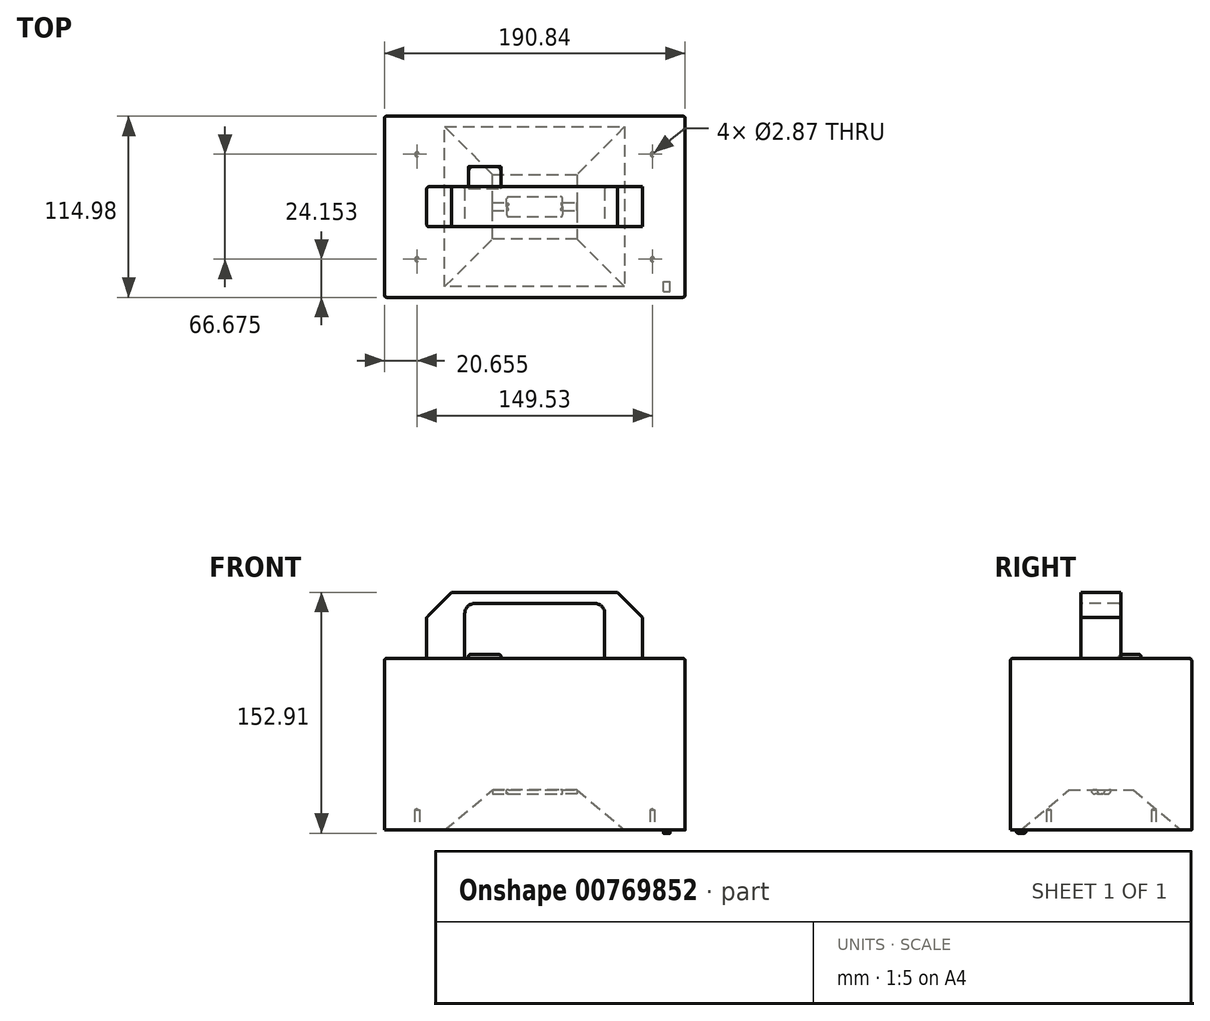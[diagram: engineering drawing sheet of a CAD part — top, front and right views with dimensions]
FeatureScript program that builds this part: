
annotation { "Feature Type Name" : "Feature", "Feature Type Description" : "" }
export const myFeature = defineFeature(function(context is Context, id is Id, definition is map)
    precondition{}
    {
        {
            var Q0;
            Q0=qCreatedBy(makeId("Top.planeOp"),FACE);
            var sketch = newSketch(context, id + "F0", { "sketchPlane" : qUnion([Q0])});
            skLineSegment(sketch, "E0.bottom", {"start": v(-95.42, 57.5) * mm, "end": v(95.42, 57.5) * mm});
            skLineSegment(sketch, "E0.top", {"start": v(-95.42, -57.5) * mm, "end": v(95.42, -57.5) * mm});
            skLineSegment(sketch, "E0.left", {"start": v(-95.42, 57.5) * mm, "end": v(-95.42, -57.5) * mm});
            skLineSegment(sketch, "E0.right", {"start": v(95.42, 57.5) * mm, "end": v(95.42, -57.5) * mm});
            skLineSegment(sketch, "E1", {"start": v(-95.42, 57.5) * mm, "end": v(95.42, -57.5) * mm, "construction": true});
            skSolve(sketch);
        }
        {
            var Q0;
            Q0 = qSketchRegion(id + "F0", true);
            extrude(context, id + "F1", {"entities" : qUnion([Q0]), "oppositeDirection" : true, "depth" : 108.97 * mm, "offsetDistance" : 25.4 * mm});
        }
        {
            var Q0;
            Q0=makeQuery(id+"F1.opExtrude","CAP_FACE",FACE,{"disambiguationData":[OSD([sQuery(id+"F0.wireOp",EDGE,"E0.bottom"),sQuery(id+"F0.wireOp",EDGE,"E0.top"),sQuery(id+"F0.wireOp",EDGE,"E0.left"),sQuery(id+"F0.wireOp",EDGE,"E0.right")])],"isStart":true});
            var sketch = newSketch(context, id + "F2", { "sketchPlane" : qUnion([Q0])});
            skLineSegment(sketch, "E2", {"start": v(-95.42, 0) * mm, "end": v(95.42, 0) * mm, "construction": true});
            skLineSegment(sketch, "E3.bottom", {"start": v(-68.58, 12.7) * mm, "end": v(68.58, 12.7) * mm});
            skLineSegment(sketch, "E3.top", {"start": v(-68.58, -12.7) * mm, "end": v(68.58, -12.7) * mm});
            skLineSegment(sketch, "E3.left", {"start": v(-68.58, 12.7) * mm, "end": v(-68.58, -12.7) * mm});
            skLineSegment(sketch, "E3.right", {"start": v(68.58, 12.7) * mm, "end": v(68.58, -12.7) * mm});
            skLineSegment(sketch, "E4", {"start": v(-68.58, 12.7) * mm, "end": v(68.58, -12.7) * mm, "construction": true});
            skPoint(sketch, "E5", {"position": v(0, 0) * mm});
            skSolve(sketch);
        }
        {
            var Q0;
            Q0 = qSketchRegion(id + "F2", true);
            extrude(context, id + "F3", {"entities" : qUnion([Q0]), "operationType" : NewBodyOperationType.ADD, "depth" : 41.9 * mm, "offsetDistance" : 25.4 * mm});
        }
        {
            var Q0;
            Q0=makeQuery(id+"F3.opExtrude","SWEPT_FACE",FACE,{"disambiguationData":[OSD([sQuery(id+"F2.wireOp",EDGE,"E3.top")])]});
            var sketch = newSketch(context, id + "F4", { "sketchPlane" : qUnion([Q0])});
            skLineSegment(sketch, "E6", {"start": v(-68.58, 26.03) * mm, "end": v(-52.7, 41.91) * mm});
            skLineSegment(sketch, "E7", {"start": v(-52.7, 41.91) * mm, "end": v(-68.58, 41.91) * mm});
            skLineSegment(sketch, "E8", {"start": v(-68.58, 41.91) * mm, "end": v(-68.58, 26.03) * mm});
            skLineSegment(sketch, "E9", {"start": v(68.58, 26.04) * mm, "end": v(52.7, 41.91) * mm});
            skLineSegment(sketch, "E10", {"start": v(52.7, 41.91) * mm, "end": v(68.58, 41.91) * mm});
            skLineSegment(sketch, "E11", {"start": v(68.58, 41.91) * mm, "end": v(68.58, 26.04) * mm});
            skLineSegment(sketch, "E12.bottom", {"start": v(-44.45, 0) * mm, "end": v(44.45, 0) * mm});
            skLineSegment(sketch, "E12.top", {"start": v(-44.45, 34.93) * mm, "end": v(44.45, 34.93) * mm});
            skLineSegment(sketch, "E12.left", {"start": v(-44.45, 0) * mm, "end": v(-44.45, 34.92) * mm});
            skLineSegment(sketch, "E12.right", {"start": v(44.45, 0) * mm, "end": v(44.45, 34.93) * mm});
            skLineSegment(sketch, "E13", {"start": v(0, 41.91) * mm, "end": v(0, 34.93) * mm, "construction": true});
            skSolve(sketch);
        }
        {
            var Q0;
            Q0 = qSketchRegion(id + "F4", true);
            extrude(context, id + "F5", {"entities" : qUnion([Q0]), "operationType" : NewBodyOperationType.REMOVE, "endBound" : BoundingType.THROUGH_ALL, "oppositeDirection" : true, "depth" : 25.4 * mm, "offsetDistance" : 25.4 * mm});
        }
        {
            var Q0;
            Q0=makeQuery(id+"F5.boolean.opBoolean","COPY",EDGE,{"derivedFrom":makeQuery(id+"F5.opExtrude","SWEPT_EDGE",EDGE,{"disambiguationData":[OSD([sQuery(id+"F2.wireOp",EDGE,"E3.top"),sQuery(id+"F2.wireOp",EDGE,"E3.left"),sQuery(id+"F4.wireOp",EDGE,"E6"),sQuery(id+"F4.wireOp",EDGE,"E8")])]})});
            var Q1;
            Q1=makeQuery(id+"F5.boolean.opBoolean","COPY",EDGE,{"derivedFrom":makeQuery(id+"F5.opExtrude","SWEPT_EDGE",EDGE,{"disambiguationData":[OSD([sQuery(id+"F2.wireOp",EDGE,"E3.top"),sQuery(id+"F4.wireOp",EDGE,"E6"),sQuery(id+"F4.wireOp",EDGE,"E7")])]})});
            var Q2;
            Q2=makeQuery(id+"F5.boolean.opBoolean","COPY",EDGE,{"derivedFrom":makeQuery(id+"F5.opExtrude","SWEPT_EDGE",EDGE,{"disambiguationData":[OSD([sQuery(id+"F2.wireOp",EDGE,"E3.top"),sQuery(id+"F4.wireOp",EDGE,"E9"),sQuery(id+"F4.wireOp",EDGE,"E10")])]})});
            var Q3;
            Q3=makeQuery(id+"F5.boolean.opBoolean","COPY",EDGE,{"derivedFrom":makeQuery(id+"F5.opExtrude","SWEPT_EDGE",EDGE,{"disambiguationData":[OSD([sQuery(id+"F2.wireOp",EDGE,"E3.top"),sQuery(id+"F2.wireOp",EDGE,"E3.right"),sQuery(id+"F4.wireOp",EDGE,"E9"),sQuery(id+"F4.wireOp",EDGE,"E11")])]})});
            var Q4;
            Q4=makeQuery(id+"F5.boolean.opBoolean","COPY",EDGE,{"derivedFrom":makeQuery(id+"F5.opExtrude","SWEPT_EDGE",EDGE,{"disambiguationData":[OSD([sQuery(id+"F4.wireOp",EDGE,"E12.top"),sQuery(id+"F4.wireOp",EDGE,"E12.left")])]})});
            var Q5;
            Q5=makeQuery(id+"F5.boolean.opBoolean","COPY",EDGE,{"derivedFrom":makeQuery(id+"F5.opExtrude","SWEPT_EDGE",EDGE,{"disambiguationData":[OSD([sQuery(id+"F4.wireOp",EDGE,"E12.top"),sQuery(id+"F4.wireOp",EDGE,"E12.right")])]})});
            fillet(context, id + "F6", {"entities" : qUnion([Q0, Q1, Q2, Q3, Q4, Q5]), "radius" : 6.35 * mm, "tangentPropagation" : true, "allowEdgeOverflow" : false});
        }
        {
            var Q0;
            Q0=makeQuery(id+"F1.opExtrude","CAP_FACE",FACE,{"disambiguationData":[OSD([sQuery(id+"F0.wireOp",EDGE,"E0.bottom"),sQuery(id+"F0.wireOp",EDGE,"E0.top"),sQuery(id+"F0.wireOp",EDGE,"E0.left"),sQuery(id+"F0.wireOp",EDGE,"E0.right")])],"isStart":false});
            var sketch = newSketch(context, id + "F7", { "sketchPlane" : qUnion([Q0])});
            skLineSegment(sketch, "E14.bottom", {"start": v(-57.15, 50.8) * mm, "end": v(57.15, 50.8) * mm});
            skLineSegment(sketch, "E14.top", {"start": v(-57.15, -50.8) * mm, "end": v(57.15, -50.8) * mm});
            skLineSegment(sketch, "E14.left", {"start": v(-57.15, 50.8) * mm, "end": v(-57.15, -50.8) * mm});
            skLineSegment(sketch, "E14.right", {"start": v(57.15, 50.8) * mm, "end": v(57.15, -50.8) * mm});
            skLineSegment(sketch, "E15", {"start": v(-95.42, 0) * mm, "end": v(95.42, 0) * mm, "construction": true});
            skLineSegment(sketch, "E16", {"start": v(-57.15, 0) * mm, "end": v(57.15, 0) * mm, "construction": true});
            skLineSegment(sketch, "E17", {"start": v(0, 50.8) * mm, "end": v(0, -50.8) * mm, "construction": true});
            skPoint(sketch, "E18", {"position": v(0, 0) * mm});
            skSolve(sketch);
        }
        {
            var Q0;
            Q0 = qSketchRegion(id + "F7", true);
            extrude(context, id + "F8", {"entities" : qUnion([Q0]), "operationType" : NewBodyOperationType.REMOVE, "oppositeDirection" : true, "depth" : 25.4 * mm, "offsetDistance" : 25.4 * mm, "hasDraft" : true, "draftAngle" : 50 * degree, "draftPullDirection" : true});
        }
        {
            var Q0;
            Q0=makeQuery(id+"F8.boolean.opBoolean","COPY",FACE,{"derivedFrom":makeQuery(id+"F8.opExtrude","CAP_FACE",FACE,{"disambiguationData":[OSD([sQuery(id+"F7.wireOp",EDGE,"E14.bottom"),sQuery(id+"F7.wireOp",EDGE,"E14.top"),sQuery(id+"F7.wireOp",EDGE,"E14.left"),sQuery(id+"F7.wireOp",EDGE,"E14.right")])],"isStart":false})});
            var sketch = newSketch(context, id + "F9", { "sketchPlane" : qUnion([Q0])});
            skLineSegment(sketch, "E19.bottom", {"start": v(-17.78, 6.35) * mm, "end": v(17.78, 6.35) * mm});
            skLineSegment(sketch, "E19.top", {"start": v(-17.78, -6.35) * mm, "end": v(17.78, -6.35) * mm});
            skLineSegment(sketch, "E19.left", {"start": v(-26.88, 2.54) * mm, "end": v(-26.88, -2.54) * mm});
            skLineSegment(sketch, "E19.right", {"start": v(26.88, 2.54) * mm, "end": v(26.88, -2.54) * mm});
            skLineSegment(sketch, "E20", {"start": v(-26.88, 2.54) * mm, "end": v(-17.78, 2.54) * mm});
            skLineSegment(sketch, "E21", {"start": v(17.78, 2.54) * mm, "end": v(26.88, 2.54) * mm});
            skLineSegment(sketch, "E22", {"start": v(-26.88, -2.54) * mm, "end": v(-17.78, -2.54) * mm});
            skLineSegment(sketch, "E23", {"start": v(17.78, -2.54) * mm, "end": v(26.88, -2.54) * mm});
            skLineSegment(sketch, "E24", {"start": v(-17.78, 2.54) * mm, "end": v(-17.78, 6.35) * mm});
            skLineSegment(sketch, "E25", {"start": v(17.78, 2.54) * mm, "end": v(17.78, 6.35) * mm});
            skLineSegment(sketch, "E26", {"start": v(-17.78, -2.54) * mm, "end": v(-17.78, -6.35) * mm});
            skLineSegment(sketch, "E27", {"start": v(17.78, -2.54) * mm, "end": v(17.78, -6.35) * mm});
            skPoint(sketch, "E28", {"position": v(-26.88, 0) * mm});
            skSolve(sketch);
        }
        {
            var Q0;
            Q0 = qSketchRegion(id + "F9", true);
            extrude(context, id + "F10", {"entities" : qUnion([Q0]), "operationType" : NewBodyOperationType.ADD, "depth" : 2.54 * mm, "offsetDistance" : 25.4 * mm});
        }
        {
            var Q0;
            Q0=makeQuery(id+"F10.opExtrude","CAP_EDGE",EDGE,{"disambiguationData":[OSD([sQuery(id+"F9.wireOp",EDGE,"E19.bottom")])],"isStart":false});
            var Q1;
            Q1=makeQuery(id+"F10.opExtrude","CAP_EDGE",EDGE,{"disambiguationData":[OSD([sQuery(id+"F9.wireOp",EDGE,"E19.top")])],"isStart":false});
            fillet(context, id + "F11", {"entities" : qUnion([Q0, Q1]), "radius" : 2.54 * mm, "tangentPropagation" : true, "allowEdgeOverflow" : false});
        }
        {
            var Q0;
            Q0=makeQuery(id+"F10.opExtrude","CAP_EDGE",EDGE,{"disambiguationData":[OSD([sQuery(id+"F9.wireOp",EDGE,"E20")])],"isStart":false});
            var Q1;
            Q1=makeQuery(id+"F10.opExtrude","CAP_EDGE",EDGE,{"disambiguationData":[OSD([sQuery(id+"F9.wireOp",EDGE,"E22")])],"isStart":false});
            var Q2;
            Q2=makeQuery(id+"F10.opExtrude","CAP_EDGE",EDGE,{"disambiguationData":[OSD([sQuery(id+"F9.wireOp",EDGE,"E23")])],"isStart":false});
            var Q3;
            Q3=makeQuery(id+"F10.opExtrude","CAP_EDGE",EDGE,{"disambiguationData":[OSD([sQuery(id+"F9.wireOp",EDGE,"E21")])],"isStart":false});
            fillet(context, id + "F12", {"entities" : qUnion([Q0, Q1, Q2, Q3]), "radius" : 2.54 * mm, "tangentPropagation" : true, "allowEdgeOverflow" : false});
        }
        {
            var Q0;
            Q0=makeQuery(id+"F10.opExtrude","CAP_EDGE",EDGE,{"disambiguationData":[OSD([sQuery(id+"F9.wireOp",EDGE,"E25")])],"isStart":false});
            var Q1;
            Q1=makeQuery(id+"F10.opExtrude","CAP_EDGE",EDGE,{"disambiguationData":[OSD([sQuery(id+"F9.wireOp",EDGE,"E27")])],"isStart":false});
            var Q2;
            Q2=makeQuery(id+"F10.opExtrude","CAP_EDGE",EDGE,{"disambiguationData":[OSD([sQuery(id+"F9.wireOp",EDGE,"E24")])],"isStart":false});
            fillet(context, id + "F13", {"entities" : qUnion([Q0, Q1, Q2]), "radius" : 1.27 * mm, "tangentPropagation" : true, "allowEdgeOverflow" : false});
        }
        {
            var Q0;
            Q0=makeQuery(id+"F1.opExtrude","CAP_FACE",FACE,{"disambiguationData":[OSD([sQuery(id+"F0.wireOp",EDGE,"E0.bottom"),sQuery(id+"F0.wireOp",EDGE,"E0.top"),sQuery(id+"F0.wireOp",EDGE,"E0.left"),sQuery(id+"F0.wireOp",EDGE,"E0.right")])],"isStart":false});
            var sketch = newSketch(context, id + "F14", { "sketchPlane" : qUnion([Q0])});
            skLineSegment(sketch, "E29.bottom", {"start": v(-74.76, 33.34) * mm, "end": v(74.76, 33.34) * mm, "construction": true});
            skLineSegment(sketch, "E29.top", {"start": v(-74.76, -33.34) * mm, "end": v(74.76, -33.34) * mm, "construction": true});
            skLineSegment(sketch, "E29.left", {"start": v(-74.76, 33.34) * mm, "end": v(-74.76, -33.34) * mm, "construction": true});
            skLineSegment(sketch, "E29.right", {"start": v(74.76, 33.34) * mm, "end": v(74.76, -33.34) * mm, "construction": true});
            skSolve(sketch);
        }
        {
            var Q0;
            Q0=sQuery(id+"F14.wireOp",VERTEX,"E29.bottom.start");
            var Q1;
            Q1=sQuery(id+"F14.wireOp",VERTEX,"E29.top.start");
            var Q2;
            Q2=sQuery(id+"F14.wireOp",VERTEX,"E29.top.end");
            var Q3;
            Q3=sQuery(id+"F14.wireOp",VERTEX,"E29.bottom.end");
            var Q4;
            Q4=makeQuery(id+"F1.opExtrude","SWEPT_BODY",BODY,{"disambiguationData":[OSD([sQuery(id+"F0.wireOp",EDGE,"E0.bottom"),sQuery(id+"F0.wireOp",EDGE,"E0.top"),sQuery(id+"F0.wireOp",EDGE,"E0.left"),sQuery(id+"F0.wireOp",EDGE,"E0.right")])]});
            hole(context, id + "F15", {"style" : HoleStyle.SIMPLE, "endStyle" : HoleEndStyle.BLIND, "standardTappedOrClearance" : lookupTablePath({ "standard" : "ANSI", "engagement" : "75%", "pitch" : "40 tpi", "size" : "#6", "type" : "Tapped" }), "standardBlindInLast" : lookupTablePath({ "standard" : "ANSI", "engagement" : "75%", "pitch" : "40 tpi", "size" : "#6", "type" : "Tapped" }), "holeDiameter" : 2.87 * mm, "majorDiameter" : 3.5 * mm, "showTappedDepth" : true, "holeDepth" : 12.7 * mm, "tappedDepth" : 10.8 * mm, "tapClearance" : 3, "locations" : qUnion([Q0, Q1, Q2, Q3]), "scope" : qUnion([Q4])});
        }
        {
            var Q0;
            Q0=makeQuery(id+"F1.opExtrude","SWEPT_EDGE",EDGE,{"disambiguationData":[OSD([sQuery(id+"F0.wireOp",EDGE,"E0.top"),sQuery(id+"F0.wireOp",EDGE,"E0.left")])]});
            var Q1;
            Q1=makeQuery(id+"F1.opExtrude","SWEPT_EDGE",EDGE,{"disambiguationData":[OSD([sQuery(id+"F0.wireOp",EDGE,"E0.bottom"),sQuery(id+"F0.wireOp",EDGE,"E0.left")])]});
            var Q2;
            Q2=makeQuery(id+"F1.opExtrude","SWEPT_EDGE",EDGE,{"disambiguationData":[OSD([sQuery(id+"F0.wireOp",EDGE,"E0.top"),sQuery(id+"F0.wireOp",EDGE,"E0.right")])]});
            var Q3;
            Q3=makeQuery(id+"F1.opExtrude","SWEPT_EDGE",EDGE,{"disambiguationData":[OSD([sQuery(id+"F0.wireOp",EDGE,"E0.bottom"),sQuery(id+"F0.wireOp",EDGE,"E0.right")])]});
            var Q4;
            Q4=makeQuery(id+"F1.opExtrude","CAP_EDGE",EDGE,{"disambiguationData":[OSD([sQuery(id+"F0.wireOp",EDGE,"E0.right")])],"isStart":true});
            var Q5;
            Q5=makeQuery(id+"F1.opExtrude","CAP_EDGE",EDGE,{"disambiguationData":[OSD([sQuery(id+"F0.wireOp",EDGE,"E0.bottom")])],"isStart":true});
            var Q6;
            Q6=makeQuery(id+"F1.opExtrude","CAP_EDGE",EDGE,{"disambiguationData":[OSD([sQuery(id+"F0.wireOp",EDGE,"E0.left")])],"isStart":true});
            var Q7;
            Q7=makeQuery(id+"F1.opExtrude","CAP_EDGE",EDGE,{"disambiguationData":[OSD([sQuery(id+"F0.wireOp",EDGE,"E0.top")])],"isStart":true});
            fillet(context, id + "F16", {"entities" : qUnion([Q0, Q1, Q2, Q3, Q4, Q5, Q6, Q7]), "radius" : 1.27 * mm, "tangentPropagation" : true, "allowEdgeOverflow" : false});
        }
        {
            var Q0;
            Q0=makeQuery(id+"F3.opExtrude","SWEPT_EDGE",EDGE,{"disambiguationData":[OSD([sQuery(id+"F2.wireOp",EDGE,"E3.top"),sQuery(id+"F2.wireOp",EDGE,"E3.left")])]});
            var Q1;
            Q1=makeQuery(id+"F3.opExtrude","SWEPT_EDGE",EDGE,{"disambiguationData":[OSD([sQuery(id+"F2.wireOp",EDGE,"E3.bottom"),sQuery(id+"F2.wireOp",EDGE,"E3.left")])]});
            var Q2;
            Q2=makeQuery(id+"F5.boolean.opBoolean","INTERSECT",EDGE,{"derivedFrom":[makeQuery(id+"F3.opExtrude","SWEPT_FACE",FACE,{"disambiguationData":[OSD([sQuery(id+"F2.wireOp",EDGE,"E3.bottom")])]}),makeQuery(id+"F5.opExtrude","SWEPT_FACE",FACE,{"disambiguationData":[OSD([sQuery(id+"F4.wireOp",EDGE,"E12.left")])]})]});
            var Q3;
            Q3=makeQuery(id+"F5.boolean.opBoolean","COPY",EDGE,{"derivedFrom":makeQuery(id+"F5.opExtrude","CAP_EDGE",EDGE,{"disambiguationData":[OSD([sQuery(id+"F4.wireOp",EDGE,"E12.left")])],"isStart":true})});
            fillet(context, id + "F17", {"entities" : qUnion([Q0, Q1, Q2, Q3]), "radius" : 1.27 * mm, "tangentPropagation" : true, "allowEdgeOverflow" : false});
        }
        {
            var Q0;
            Q0=makeQuery(id+"F5.boolean.opBoolean","MERGE",FACE,{"derivedFrom":[makeQuery(id+"F1.opExtrude","CAP_FACE",FACE,{"disambiguationData":[OSD([sQuery(id+"F0.wireOp",EDGE,"E0.bottom"),sQuery(id+"F0.wireOp",EDGE,"E0.top"),sQuery(id+"F0.wireOp",EDGE,"E0.left"),sQuery(id+"F0.wireOp",EDGE,"E0.right")])],"isStart":true}),makeQuery(id+"F5.opExtrude","SWEPT_FACE",FACE,{"disambiguationData":[OSD([sQuery(id+"F4.wireOp",EDGE,"E12.bottom")])]})]});
            var sketch = newSketch(context, id + "F18", { "sketchPlane" : qUnion([Q0])});
            skLineSegment(sketch, "E30.bottom", {"start": v(-42.08, 25.4) * mm, "end": v(-21.5, 25.4) * mm});
            skLineSegment(sketch, "E30.top", {"start": v(-42.08, 11.43) * mm, "end": v(-21.5, 11.43) * mm});
            skLineSegment(sketch, "E30.left", {"start": v(-42.08, 25.4) * mm, "end": v(-42.08, 11.43) * mm});
            skLineSegment(sketch, "E30.right", {"start": v(-21.5, 25.4) * mm, "end": v(-21.5, 11.43) * mm});
            skSolve(sketch);
        }
        {
            var Q0;
            Q0 = qSketchRegion(id + "F18", true);
            extrude(context, id + "F19", {"entities" : qUnion([Q0]), "operationType" : NewBodyOperationType.ADD, "depth" : 2.54 * mm, "offsetDistance" : 25.4 * mm});
        }
        {
            var Q0;
            Q0=makeQuery(id+"F19.opExtrude","CAP_EDGE",EDGE,{"disambiguationData":[OSD([sQuery(id+"F18.wireOp",EDGE,"E30.bottom")])],"isStart":false});
            var Q1;
            Q1=makeQuery(id+"F19.opExtrude","CAP_EDGE",EDGE,{"disambiguationData":[OSD([sQuery(id+"F18.wireOp",EDGE,"E30.left")])],"isStart":false});
            var Q2;
            Q2=makeQuery(id+"F19.opExtrude","CAP_EDGE",EDGE,{"disambiguationData":[OSD([sQuery(id+"F18.wireOp",EDGE,"E30.top")])],"isStart":false});
            var Q3;
            Q3=makeQuery(id+"F19.opExtrude","CAP_EDGE",EDGE,{"disambiguationData":[OSD([sQuery(id+"F18.wireOp",EDGE,"E30.right")])],"isStart":false});
            fillet(context, id + "F20", {"entities" : qUnion([Q0, Q1, Q2, Q3]), "radius" : 1.27 * mm, "tangentPropagation" : true, "allowEdgeOverflow" : false});
        }
        {
            var Q0;
            Q0=makeQuery(id+"F1.opExtrude","CAP_FACE",FACE,{"disambiguationData":[OSD([sQuery(id+"F0.wireOp",EDGE,"E0.bottom"),sQuery(id+"F0.wireOp",EDGE,"E0.top"),sQuery(id+"F0.wireOp",EDGE,"E0.left"),sQuery(id+"F0.wireOp",EDGE,"E0.right")])],"isStart":false});
            var sketch = newSketch(context, id + "F21", { "sketchPlane" : qUnion([Q0])});
            skLineSegment(sketch, "E31.bottom", {"start": v(81.74, 53.94) * mm, "end": v(86.02, 53.94) * mm});
            skLineSegment(sketch, "E31.top", {"start": v(81.74, 47.59) * mm, "end": v(86.02, 47.59) * mm});
            skLineSegment(sketch, "E31.left", {"start": v(81.74, 53.94) * mm, "end": v(81.74, 47.59) * mm});
            skLineSegment(sketch, "E31.right", {"start": v(86.02, 53.94) * mm, "end": v(86.02, 47.59) * mm});
            skSolve(sketch);
        }
        {
            var Q0;
            Q0 = qSketchRegion(id + "F21", true);
            extrude(context, id + "F22", {"entities" : qUnion([Q0]), "operationType" : NewBodyOperationType.ADD, "depth" : 2.03 * mm, "offsetDistance" : 25.4 * mm});
        }
        {
            var Q0;
            Q0=makeQuery(id+"F22.opExtrude","CAP_EDGE",EDGE,{"disambiguationData":[OSD([sQuery(id+"F21.wireOp",EDGE,"E31.bottom")])],"isStart":false});
            var Q1;
            Q1=makeQuery(id+"F22.opExtrude","CAP_EDGE",EDGE,{"disambiguationData":[OSD([sQuery(id+"F21.wireOp",EDGE,"E31.top")])],"isStart":false});
            fillet(context, id + "F23", {"entities" : qUnion([Q0, Q1]), "radius" : 1.27 * mm, "tangentPropagation" : true, "allowEdgeOverflow" : false});
        }
    });
